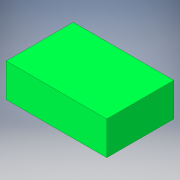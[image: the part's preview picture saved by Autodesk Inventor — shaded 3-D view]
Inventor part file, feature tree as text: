
AUTODESK INVENTOR PART (.ipt)
format: ipt  version: 2016 (Build 200138000, 138)  size: 96,768 bytes
history: native  units: in
note: dims shown in document units (in); Inventor stores cm internally (conversion verified against a paired STEP export)
features: extrude x1, sketch x1
ambient origin geometry x8: Origin, YZ Plane, XZ Plane, XY Plane, X Axis, Y Axis, Z Axis, Center Point
bodies: Solid1 (feature_tree)
feature tree (2):
  extrude  "Extrusion1"  Depth=1.0in
  sketch  "Sketch1"  dims[d0=3.0in d1=1.0in d2=2.0in d3=0.0in]
